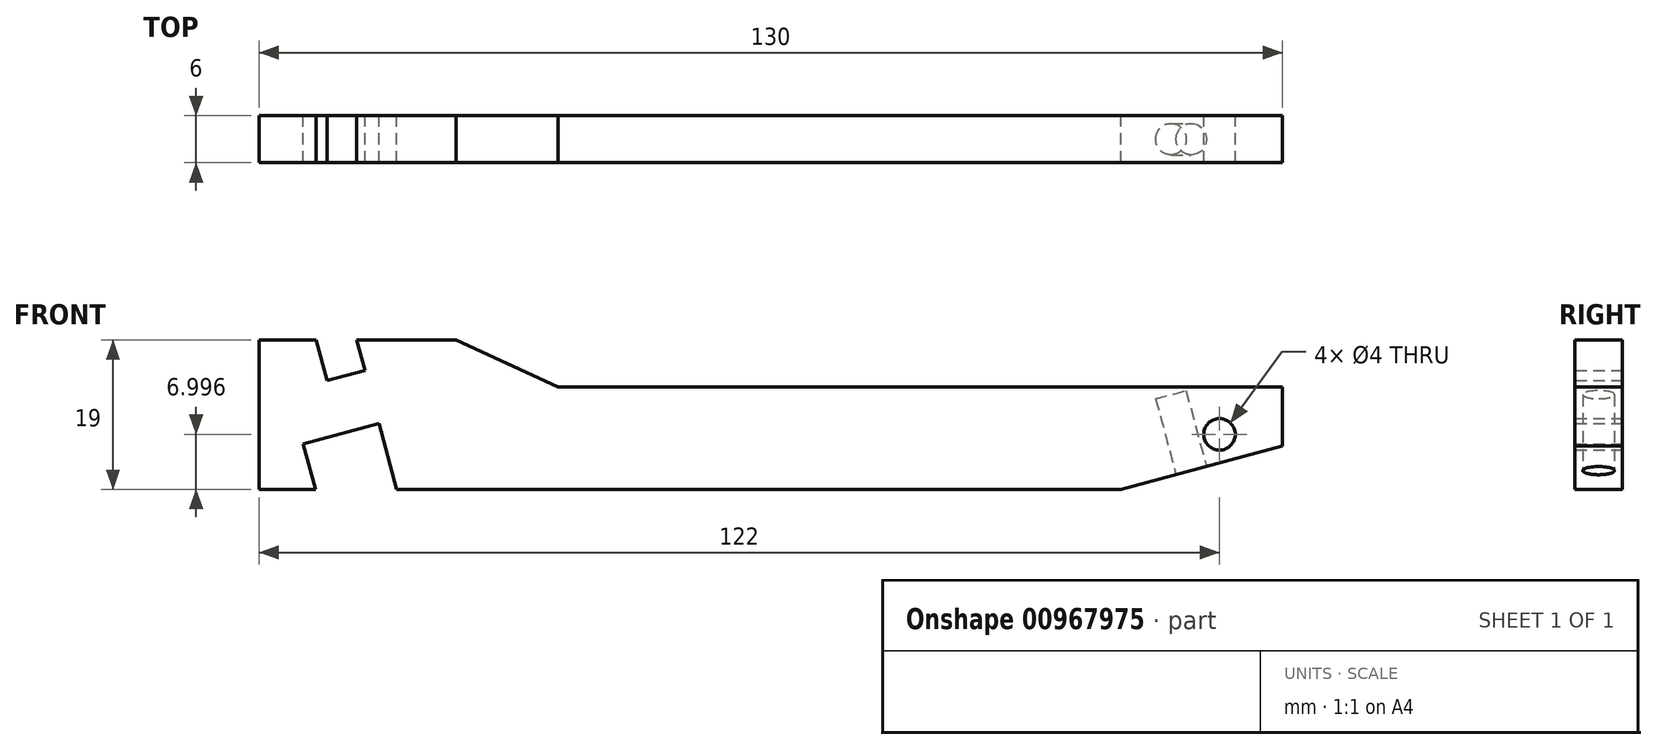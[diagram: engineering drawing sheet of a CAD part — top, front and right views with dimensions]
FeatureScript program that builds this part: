
annotation { "Feature Type Name" : "Feature", "Feature Type Description" : "" }
export const myFeature = defineFeature(function(context is Context, id is Id, definition is map)
    precondition{}
    {
        {
            var Q0;
            Q0=qCreatedBy(makeId("Front.planeOp"),FACE);
            var sketch = newSketch(context, id + "F0", { "sketchPlane" : qUnion([Q0])});
            skLineSegment(sketch, "E0", {"start": v(-45.87, 10.62) * mm, "end": v(-45.87, -8.38) * mm});
            skLineSegment(sketch, "E1", {"start": v(84.13, -2.9) * mm, "end": v(84.13, 4.62) * mm});
            skLineSegment(sketch, "E2", {"start": v(84.13, 4.62) * mm, "end": v(-7.87, 4.62) * mm});
            skLineSegment(sketch, "E3", {"start": v(-7.87, 4.62) * mm, "end": v(-20.87, 10.62) * mm});
            skLineSegment(sketch, "E4", {"start": v(-33.46, 10.62) * mm, "end": v(-32.43, 6.75) * mm});
            skLineSegment(sketch, "E5", {"start": v(-32.43, 6.75) * mm, "end": v(-37.25, 5.46) * mm});
            skLineSegment(sketch, "E6", {"start": v(-37.25, 5.46) * mm, "end": v(-38.64, 10.62) * mm});
            skLineSegment(sketch, "E7", {"start": v(-30.62, 0) * mm, "end": v(-40.28, -2.59) * mm});
            skLineSegment(sketch, "E8", {"start": v(-40.28, -2.59) * mm, "end": v(-38.72, -8.38) * mm});
            skLineSegment(sketch, "E9.trimOffspring", {"start": v(-30.62, 0) * mm, "end": v(-28.37, -8.38) * mm});
            skLineSegment(sketch, "E10", {"start": v(-45.87, -8.38) * mm, "end": v(-38.72, -8.38) * mm});
            skLineSegment(sketch, "E11", {"start": v(-45.87, 10.62) * mm, "end": v(-38.64, 10.62) * mm});
            skLineSegment(sketch, "E12", {"start": v(-33.46, 10.62) * mm, "end": v(-20.87, 10.62) * mm});
            skLineSegment(sketch, "E13", {"start": v(-28.37, -8.38) * mm, "end": v(63.63, -8.38) * mm});
            skLineSegment(sketch, "E14", {"start": v(63.63, -8.38) * mm, "end": v(84.13, -2.9) * mm});
            skSolve(sketch);
        }
        {
            var Q0;
            Q0 = qSketchRegion(id + "F0", true);
            extrude(context, id + "F1", {"entities" : qUnion([Q0]), "depth" : 6 * mm, "offsetDistance" : 25 * mm});
        }
        {
            var Q0;
            Q0=qCreatedBy(makeId("Front.planeOp"),FACE);
            var sketch = newSketch(context, id + "F2", { "sketchPlane" : qUnion([Q0])});
            skCircle(sketch, "E15", {"center": v(76.13, -1.38) * mm, "radius": 2 * mm});
            skSolve(sketch);
        }
        {
            var Q0;
            Q0 = qSketchRegion(id + "F2", true);
            var Q1;
            Q1=makeQuery(id+"F1.opExtrude","CAP_FACE",FACE,{"disambiguationData":[OSD([sQuery(id+"F0.wireOp",EDGE,"E0"),sQuery(id+"F0.wireOp",EDGE,"E1"),sQuery(id+"F0.wireOp",EDGE,"E2"),sQuery(id+"F0.wireOp",EDGE,"E3"),sQuery(id+"F0.wireOp",EDGE,"E4"),sQuery(id+"F0.wireOp",EDGE,"E5"),sQuery(id+"F0.wireOp",EDGE,"E6"),sQuery(id+"F0.wireOp",EDGE,"E7"),sQuery(id+"F0.wireOp",EDGE,"E8"),sQuery(id+"F0.wireOp",EDGE,"E9.trimOffspring"),sQuery(id+"F0.wireOp",EDGE,"E10"),sQuery(id+"F0.wireOp",EDGE,"E11"),sQuery(id+"F0.wireOp",EDGE,"E12"),sQuery(id+"F0.wireOp",EDGE,"E13"),sQuery(id+"F0.wireOp",EDGE,"E14")])],"isStart":false});
            extrude(context, id + "F3", {"entities" : qUnion([Q0, Q1]), "operationType" : NewBodyOperationType.REMOVE, "depth" : 25 * mm, "offsetDistance" : 25 * mm});
        }
        {
            var Q0;
            Q0=makeQuery(id+"F1.opExtrude","SWEPT_FACE",FACE,{"disambiguationData":[OSD([sQuery(id+"F0.wireOp",EDGE,"E14")])]});
            var sketch = newSketch(context, id + "F4", { "sketchPlane" : qUnion([Q0])});
            skCircle(sketch, "E16", {"center": v(68.52, 3) * mm, "radius": 2 * mm});
            skSolve(sketch);
        }
        {
            var Q0;
            Q0 = qSketchRegion(id + "F4", true);
            extrude(context, id + "F5", {"entities" : qUnion([Q0]), "operationType" : NewBodyOperationType.REMOVE, "oppositeDirection" : true, "depth" : 10 * mm, "offsetDistance" : 25 * mm});
        }
    });
